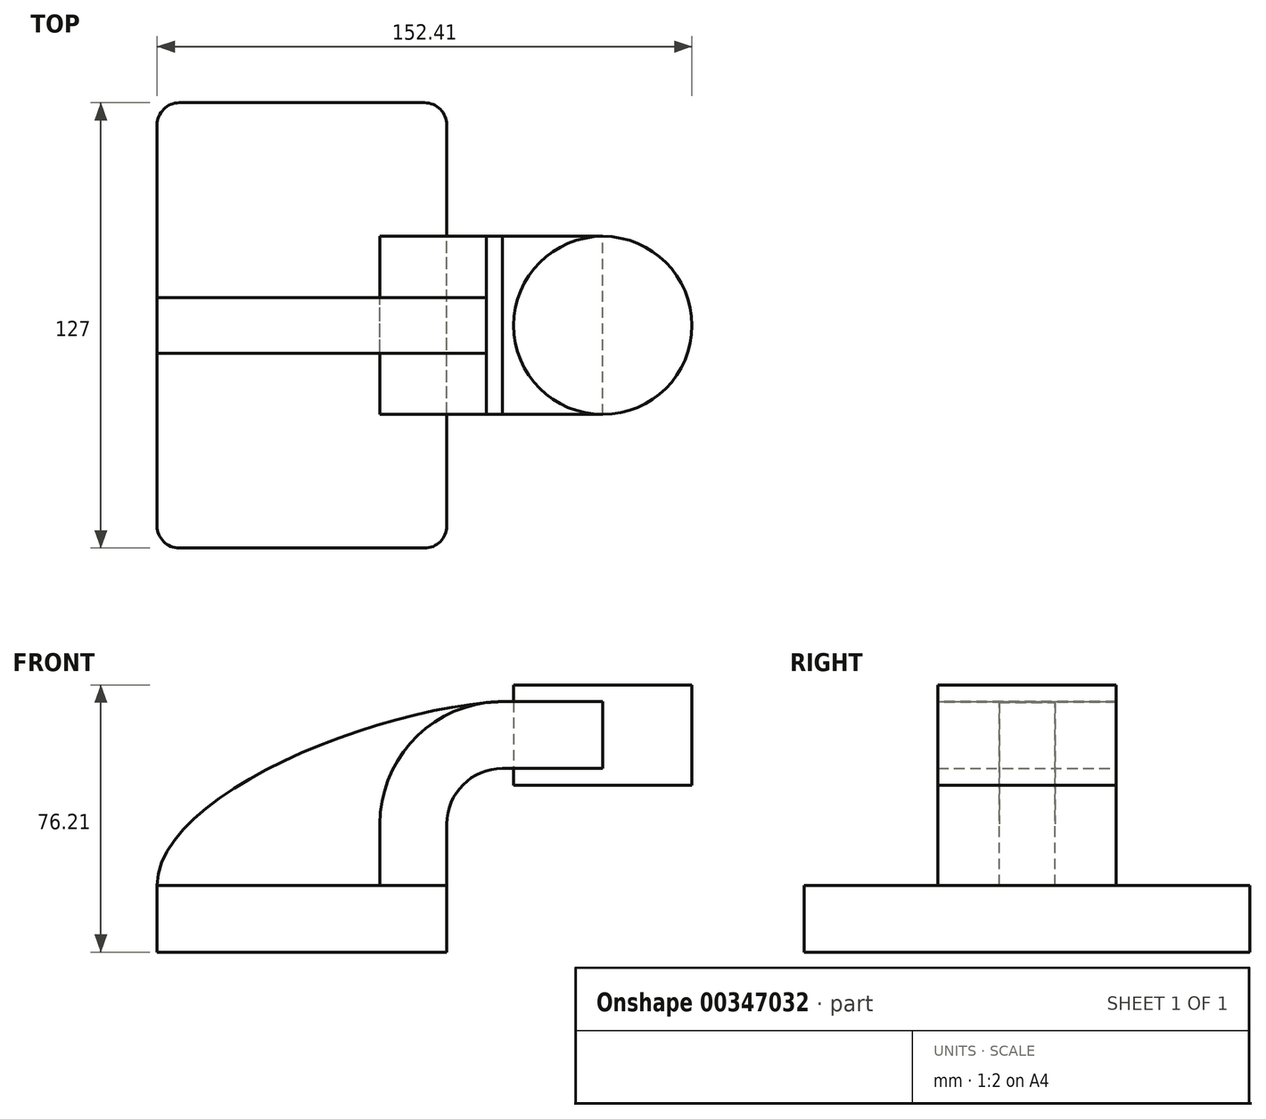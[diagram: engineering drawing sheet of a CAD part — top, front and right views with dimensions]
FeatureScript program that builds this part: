
annotation { "Feature Type Name" : "Feature", "Feature Type Description" : "" }
export const myFeature = defineFeature(function(context is Context, id is Id, definition is map)
    precondition{}
    {
        {
            var Q0;
            Q0=qCreatedBy(makeId("Front.planeOp"),FACE);
            var sketch = newSketch(context, id + "F0", { "sketchPlane" : qUnion([Q0])});
            skLineSegment(sketch, "E0.bottom", {"start": v(-41.27, 9.53) * mm, "end": v(41.27, 9.53) * mm});
            skLineSegment(sketch, "E0.top", {"start": v(-41.27, -9.52) * mm, "end": v(41.27, -9.52) * mm});
            skLineSegment(sketch, "E0.left", {"start": v(-41.28, 9.53) * mm, "end": v(-41.28, -9.53) * mm});
            skLineSegment(sketch, "E0.right", {"start": v(41.28, 9.53) * mm, "end": v(41.28, -9.53) * mm});
            skPoint(sketch, "E0.middle", {"position": v(0, 0) * mm});
            skLineSegment(sketch, "E1.bottom", {"start": v(60.33, 66.68) * mm, "end": v(111.13, 66.68) * mm});
            skLineSegment(sketch, "E1.top", {"start": v(60.33, 38.1) * mm, "end": v(111.13, 38.1) * mm});
            skLineSegment(sketch, "E1.left", {"start": v(60.33, 66.67) * mm, "end": v(60.33, 38.1) * mm});
            skLineSegment(sketch, "E1.right", {"start": v(111.13, 66.67) * mm, "end": v(111.13, 38.1) * mm});
            skPoint(sketch, "E1.middle", {"position": v(85.73, 52.39) * mm});
            skLineSegment(sketch, "E2", {"start": v(41.28, 9.53) * mm, "end": v(41.28, 26.99) * mm});
            skArc(sketch, "E3", {"start": v(41.28, 26.99) * mm, "mid": v(45.92, 38.21) * mm, "end": v(57.15, 42.86) * mm});
            skLineSegment(sketch, "E4", {"start": v(57.15, 42.86) * mm, "end": v(85.73, 42.86) * mm});
            skLineSegment(sketch, "E5.0", {"start": v(57.15, 61.91) * mm, "end": v(86.3, 61.91) * mm});
            skArc(sketch, "E5.1", {"start": v(22.23, 26.99) * mm, "mid": v(32.45, 51.68) * mm, "end": v(57.15, 61.91) * mm});
            skLineSegment(sketch, "E5.2", {"start": v(22.23, 9.53) * mm, "end": v(22.23, 26.99) * mm});
            skLineSegment(sketch, "E6", {"start": v(85.73, 38.1) * mm, "end": v(85.73, 66.68) * mm});
            skFitSpline(sketch, "E7", {"points": [v(-41.28, 9.53) * mm, v(57.15, 61.91) * mm], "startDerivative": vector(0.12, 77.91) * mm, "endDerivative": vector(105.27, 4.2) * mm});
            skSolve(sketch);
        }
        {
            var Q0;
            Q0=makeQuery(id+"F0.imprint","IMPRINT",FACE,{"disambiguationData":[TD([[makeQuery(id+"F0.imprint","IMPRINT",EDGE,{"derivedFrom":sQuery(id+"F0.wireOp",EDGE,"E0.top")}),1.0]])]});
            extrude(context, id + "F1", {"entities" : qUnion([Q0]), "endBound" : BoundingType.SYMMETRIC, "depth" : 127 * mm});
        }
        {
            var Q0;
            {var subQ4=sQuery(id+"F0.wireOp",EDGE,"E1.right");Q0=makeQuery(id+"F0.imprint","IMPRINT",FACE,{"disambiguationData":[TD([[makeQuery(id+"F0.imprint","IMPRINT",EDGE,{"derivedFrom":subQ4}),-1.0]])]});}
            var Q1;
            Q1=sQuery(id+"F0.wireOp",EDGE,"E6");
            revolve(context, id + "F2", {"entities" : qUnion([Q0]), "axis" : qUnion([Q1]), "revolveType" : RevolveType.FULL});
        }
        {
            var Q0;
            {var subQ3=sQuery(id+"F0.wireOp",EDGE,"E5.2");Q0=makeQuery(id+"F0.imprint","IMPRINT",FACE,{"disambiguationData":[TD([[makeQuery(id+"F0.imprint","IMPRINT",EDGE,{"derivedFrom":subQ3}),1.0]])]});}
            extrude(context, id + "F3", {"entities" : qUnion([Q0]), "endBound" : BoundingType.SYMMETRIC, "depth" : 15.88 * mm});
        }
        {
            var Q0;
            {var subQ0=sQuery(id+"F0.wireOp",EDGE,"E5.0");var subQ1=sQuery(id+"F0.wireOp",EDGE,"E1.left");var subQ2=makeQuery(id+"F0.imprint","INTERSECT",VERTEX,{"derivedFrom":[subQ1,subQ0]});Q0=makeQuery(id+"F0.imprint","IMPRINT",FACE,{"disambiguationData":[TD([[makeQuery(id+"F0.imprint","IMPRINT",EDGE,{"disambiguationData":[TD([[subQ2,-1.0]])],"derivedFrom":subQ1}),1.0]])]});}
            var Q1;
            {var subQ1=sQuery(id+"F0.wireOp",EDGE,"E2");Q1=makeQuery(id+"F0.imprint","IMPRINT",FACE,{"disambiguationData":[TD([[makeQuery(id+"F0.imprint","IMPRINT",EDGE,{"derivedFrom":subQ1}),1.0]])]});}
            extrude(context, id + "F4", {"entities" : qUnion([Q0, Q1]), "endBound" : BoundingType.SYMMETRIC, "depth" : 50.8 * mm});
        }
        {
            var Q0;
            Q0=makeQuery(id+"F1.opExtrude","CAP_EDGE",EDGE,{"disambiguationData":[OSD([sQuery(id+"F0.wireOp",EDGE,"E0.right")])],"isStart":false});
            var Q1;
            Q1=makeQuery(id+"F1.opExtrude","CAP_EDGE",EDGE,{"disambiguationData":[OSD([sQuery(id+"F0.wireOp",EDGE,"E0.left")])],"isStart":false});
            var Q2;
            Q2=makeQuery(id+"F1.opExtrude","CAP_EDGE",EDGE,{"disambiguationData":[OSD([sQuery(id+"F0.wireOp",EDGE,"E0.right")])],"isStart":true});
            var Q3;
            Q3=makeQuery(id+"F1.opExtrude","CAP_EDGE",EDGE,{"disambiguationData":[OSD([sQuery(id+"F0.wireOp",EDGE,"E0.left")])],"isStart":true});
            fillet(context, id + "F5", {"entities" : qUnion([Q0, Q1, Q2, Q3]), "radius" : 6.35 * mm, "tangentPropagation" : true, "allowEdgeOverflow" : false});
        }
    });
